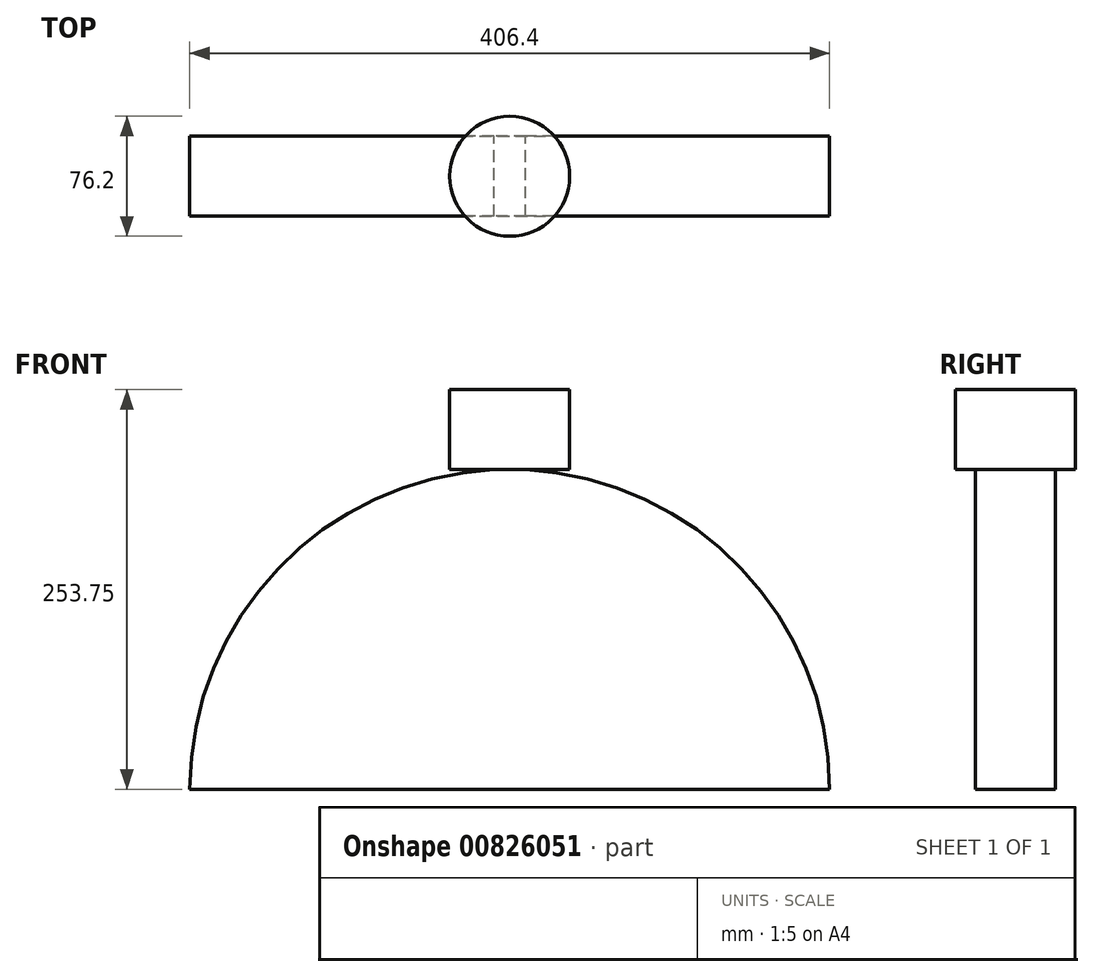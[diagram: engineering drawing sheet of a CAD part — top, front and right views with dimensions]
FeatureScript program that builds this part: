
annotation { "Feature Type Name" : "Feature", "Feature Type Description" : "" }
export const myFeature = defineFeature(function(context is Context, id is Id, definition is map)
    precondition{}
    {
        {
            var Q0;
            Q0=qCreatedBy(makeId("Front.planeOp"),FACE);
            var sketch = newSketch(context, id + "F0", { "sketchPlane" : qUnion([Q0])});
            skLineSegment(sketch, "E0", {"start": v(0, 0) * mm, "end": v(406.4, 0) * mm});
            skArc(sketch, "E1", {"start": v(406.4, 0) * mm, "mid": v(203.2, 203.2) * mm, "end": v(0, 0) * mm});
            skSolve(sketch);
        }
        {
            var Q0;
            Q0=makeQuery(id+"F0.imprint","IMPRINT",FACE,{"disambiguationData":[TD([[makeQuery(id+"F0.imprint","IMPRINT",EDGE,{"derivedFrom":sQuery(id+"F0.wireOp",EDGE,"E0")}),1.0]])]});
            extrude(context, id + "F1", {"entities" : qUnion([Q0]), "depth" : 50.8 * mm, "offsetDistance" : 25.4 * mm});
        }
        {
            var Q0;
            Q0=qCreatedBy(makeId("Top.planeOp"),FACE);
            cPlane(context, id + "F2", {"entities" : qUnion([Q0]), "cplaneType" : CPlaneType.OFFSET, "offset" : 202.95 * mm, "width" : 152.4 * mm, "height" : 152.4 * mm});
        }
        {
            var Q0;
            Q0=qCreatedBy(id+"F2.planeOp",FACE);
            var sketch = newSketch(context, id + "F3", { "sketchPlane" : qUnion([Q0])});
            skLineSegment(sketch, "E2", {"start": v(0, 0) * mm, "end": v(203.2, 0) * mm});
            skLineSegment(sketch, "E3", {"start": v(203.2, 0) * mm, "end": v(203.2, -25.4) * mm});
            skCircle(sketch, "E4", {"center": v(203.2, -25.4) * mm, "radius": 38.1 * mm});
            skSolve(sketch);
        }
        {
            var Q0;
            Q0 = qSketchRegion(id + "F3", true);
            extrude(context, id + "F4", {"entities" : qUnion([Q0]), "operationType" : NewBodyOperationType.ADD, "depth" : 50.8 * mm, "offsetDistance" : 25.4 * mm});
        }
    });
